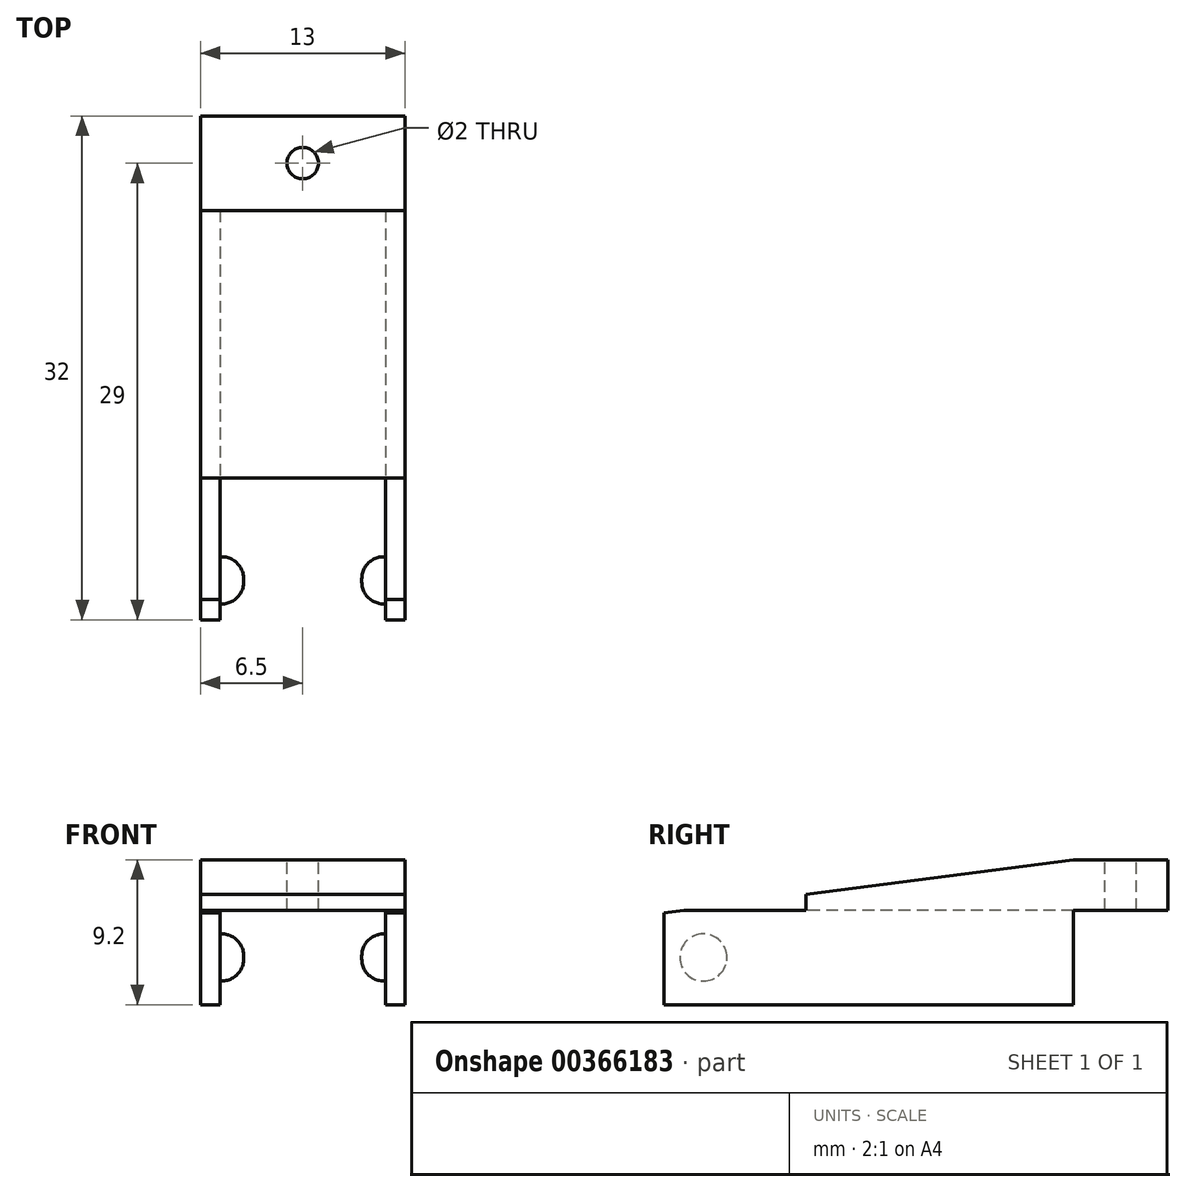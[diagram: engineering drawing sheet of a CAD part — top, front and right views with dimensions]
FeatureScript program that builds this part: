
annotation { "Feature Type Name" : "Feature", "Feature Type Description" : "" }
export const myFeature = defineFeature(function(context is Context, id is Id, definition is map)
    precondition{}
    {
        {
            var Q0;
            Q0=qCreatedBy(makeId("Right.planeOp"),FACE);
            var sketch = newSketch(context, id + "F0", { "sketchPlane" : qUnion([Q0])});
            skLineSegment(sketch, "E0", {"start": v(0, 0) * mm, "end": v(-17, 0) * mm});
            skLineSegment(sketch, "E1", {"start": v(-17, 0) * mm, "end": v(-17, 1) * mm});
            skLineSegment(sketch, "E2", {"start": v(-17, 1) * mm, "end": v(0, 3.2) * mm});
            skLineSegment(sketch, "E3", {"start": v(0, 3.2) * mm, "end": v(6, 3.2) * mm});
            skLineSegment(sketch, "E4", {"start": v(6, 3.2) * mm, "end": v(6, 0) * mm});
            skLineSegment(sketch, "E5", {"start": v(6, 0) * mm, "end": v(0, 0) * mm});
            skLineSegment(sketch, "E6.bottom", {"start": v(0, 0) * mm, "end": v(-26, 0) * mm});
            skLineSegment(sketch, "E6.top", {"start": v(0, -6) * mm, "end": v(-26, -6) * mm});
            skLineSegment(sketch, "E6.left", {"start": v(0, 0) * mm, "end": v(0, -6) * mm});
            skLineSegment(sketch, "E6.right", {"start": v(-26, 0) * mm, "end": v(-26, -6) * mm});
            skSolve(sketch);
        }
        {
            var Q0;
            Q0=makeQuery(id+"F0.imprint","IMPRINT",FACE,{"disambiguationData":[TD([[makeQuery(id+"F0.imprint","IMPRINT",EDGE,{"derivedFrom":sQuery(id+"F0.wireOp",EDGE,"E6.top")}),-1.0]])]});
            var Q1;
            {var subQ0=sQuery(id+"F0.wireOp",EDGE,"E1");Q1=makeQuery(id+"F0.imprint","IMPRINT",FACE,{"disambiguationData":[TD([[makeQuery(id+"F0.imprint","IMPRINT",EDGE,{"derivedFrom":subQ0}),-1.0]])]});}
            extrude(context, id + "F1", {"entities" : qUnion([Q0, Q1]), "depth" : 13 * mm});
        }
        {
            var Q0;
            Q0=makeQuery(id+"F1.opExtrude","SWEPT_FACE",FACE,{"disambiguationData":[OSD([sQuery(id+"F0.wireOp",EDGE,"E3")])]});
            var sketch = newSketch(context, id + "F2", { "sketchPlane" : qUnion([Q0])});
            skCircle(sketch, "E7", {"center": v(6.5, 3) * mm, "radius": 1 * mm});
            skSolve(sketch);
        }
        {
            var Q0;
            Q0=makeQuery(id+"F2.imprint","IMPRINT",FACE,{"disambiguationData":[TD([[makeQuery(id+"F2.imprint","IMPRINT",EDGE,{"derivedFrom":sQuery(id+"F2.wireOp",EDGE,"E7")}),1.0]])]});
            extrude(context, id + "F3", {"entities" : qUnion([Q0]), "operationType" : NewBodyOperationType.REMOVE, "endBound" : BoundingType.THROUGH_ALL, "oppositeDirection" : true, "depth" : 25 * mm});
        }
        {
            var Q0;
            Q0=makeQuery(id+"F1.opExtrude","SWEPT_FACE",FACE,{"disambiguationData":[OSD([sQuery(id+"F0.wireOp",EDGE,"E6.right")])]});
            var sketch = newSketch(context, id + "F4", { "sketchPlane" : qUnion([Q0])});
            skLineSegment(sketch, "E8.bottom", {"start": v(1.25, -6) * mm, "end": v(11.75, -6) * mm});
            skLineSegment(sketch, "E8.top", {"start": v(1.25, 0) * mm, "end": v(11.75, 0) * mm});
            skLineSegment(sketch, "E8.left", {"start": v(1.25, -6) * mm, "end": v(1.25, 0) * mm});
            skLineSegment(sketch, "E8.right", {"start": v(11.75, -6) * mm, "end": v(11.75, 0) * mm});
            skSolve(sketch);
        }
        {
            var Q0;
            Q0=makeQuery(id+"F4.imprint","IMPRINT",FACE,{"disambiguationData":[TD([[makeQuery(id+"F4.imprint","IMPRINT",EDGE,{"derivedFrom":sQuery(id+"F4.wireOp",EDGE,"E8.bottom")}),-1.0]])]});
            extrude(context, id + "F5", {"entities" : qUnion([Q0]), "operationType" : NewBodyOperationType.REMOVE, "endBound" : BoundingType.THROUGH_ALL, "oppositeDirection" : true, "depth" : 25 * mm});
        }
        {
            var Q0;
            Q0=makeQuery(id+"F5.boolean.opBoolean","COPY",FACE,{"derivedFrom":makeQuery(id+"F5.opExtrude","SWEPT_FACE",FACE,{"disambiguationData":[OSD([sQuery(id+"F4.wireOp",EDGE,"E8.left")])]})});
            var sketch = newSketch(context, id + "F6", { "sketchPlane" : qUnion([Q0])});
            skCircle(sketch, "E9", {"center": v(-23.5, -3) * mm, "radius": 1.5 * mm});
            skSolve(sketch);
        }
        {
            var Q0;
            Q0 = qSketchRegion(id + "F6", true);
            extrude(context, id + "F7", {"entities" : qUnion([Q0]), "operationType" : NewBodyOperationType.ADD, "depth" : 1.5 * mm});
        }
        {
            var Q0;
            Q0=makeQuery(id+"F7.opExtrude","CAP_EDGE",EDGE,{"disambiguationData":[OSD([sQuery(id+"F6.wireOp",EDGE,"E9")])],"isStart":false});
            fillet(context, id + "F8", {"entities" : qUnion([Q0]), "radius" : 1.4 * mm, "tangentPropagation" : true, "allowEdgeOverflow" : false});
        }
        {
            var Q0;
            Q0=makeQuery(id+"F5.boolean.opBoolean","COPY",FACE,{"derivedFrom":makeQuery(id+"F5.opExtrude","SWEPT_FACE",FACE,{"disambiguationData":[OSD([sQuery(id+"F4.wireOp",EDGE,"E8.right")])]})});
            var sketch = newSketch(context, id + "F9", { "sketchPlane" : qUnion([Q0])});
            skCircle(sketch, "E10", {"center": v(23.5, -3) * mm, "radius": 1.5 * mm});
            skSolve(sketch);
        }
        {
            var Q0;
            Q0 = qSketchRegion(id + "F9", true);
            extrude(context, id + "F10", {"entities" : qUnion([Q0]), "operationType" : NewBodyOperationType.ADD, "depth" : 1.5 * mm});
        }
        {
            var Q0;
            Q0=makeQuery(id+"F10.opExtrude","CAP_EDGE",EDGE,{"disambiguationData":[OSD([sQuery(id+"F9.wireOp",EDGE,"E10")])],"isStart":false});
            fillet(context, id + "F11", {"entities" : qUnion([Q0]), "radius" : 1.4 * mm, "tangentPropagation" : true, "allowEdgeOverflow" : false});
        }
        {
            var Q0;
            Q0=makeQuery(id+"F1.opExtrude","CAP_FACE",FACE,{"disambiguationData":[OSD([sQuery(id+"F0.wireOp",EDGE,"E1"),sQuery(id+"F0.wireOp",EDGE,"E2"),sQuery(id+"F0.wireOp",EDGE,"E3"),sQuery(id+"F0.wireOp",EDGE,"E4"),sQuery(id+"F0.wireOp",EDGE,"E5"),sQuery(id+"F0.wireOp",EDGE,"E6.bottom"),sQuery(id+"F0.wireOp",EDGE,"E6.top"),sQuery(id+"F0.wireOp",EDGE,"E6.left"),sQuery(id+"F0.wireOp",EDGE,"E6.right")])],"isStart":true});
            var sketch = newSketch(context, id + "F12", { "sketchPlane" : qUnion([Q0])});
            skLineSegment(sketch, "E11", {"start": v(0, 3.2) * mm, "end": v(30.15, -0.7) * mm});
            skSolve(sketch);
        }
        {
            var Q0;
            {var subQ0=sQuery(id+"F12.wireOp",EDGE,"E11");var subQ1=makeQuery(id+"F1.opExtrude","CAP_EDGE",EDGE,{"disambiguationData":[OSD([sQuery(id+"F0.wireOp",EDGE,"E6.right")])],"isStart":true});var subQ2=makeQuery(id+"F12.imprint","INTERSECT",VERTEX,{"derivedFrom":[subQ1,subQ0]});Q0=makeQuery(id+"F12.imprint","IMPRINT",FACE,{"disambiguationData":[TD([[makeQuery(id+"F12.imprint","IMPRINT",EDGE,{"disambiguationData":[TD([[subQ2,1.0]])],"derivedFrom":subQ0}),1.0]])]});}
            extrude(context, id + "F13", {"entities" : qUnion([Q0]), "operationType" : NewBodyOperationType.REMOVE, "endBound" : BoundingType.THROUGH_ALL, "oppositeDirection" : true, "depth" : 25 * mm});
        }
    });
